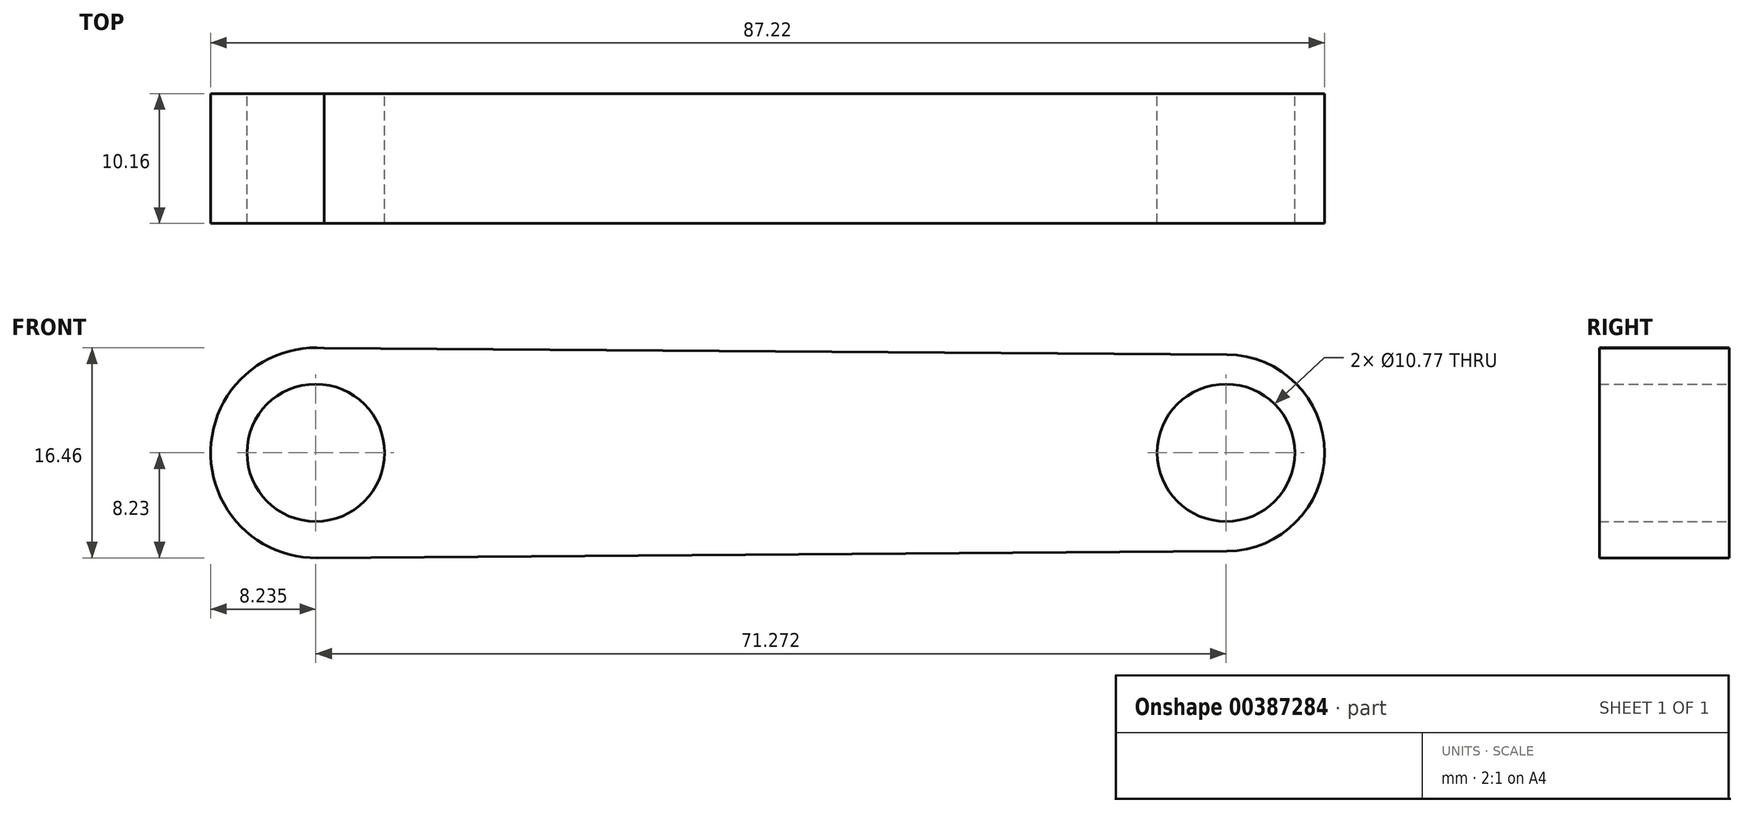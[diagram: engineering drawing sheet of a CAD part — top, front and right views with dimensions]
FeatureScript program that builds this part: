
annotation { "Feature Type Name" : "Feature", "Feature Type Description" : "" }
export const myFeature = defineFeature(function(context is Context, id is Id, definition is map)
    precondition{}
    {
        {
            var Q0;
            Q0=qCreatedBy(makeId("Front.planeOp"),FACE);
            var sketch = newSketch(context, id + "F0", { "sketchPlane" : qUnion([Q0])});
            skCircle(sketch, "E0", {"center": v(-39.6, 0) * mm, "radius": 5.39 * mm});
            skCircle(sketch, "E1", {"center": v(31.68, 0) * mm, "radius": 5.39 * mm});
            skArc(sketch, "E2", {"start": v(-38.94, 8.2) * mm, "mid": v(-47.82, 0.26) * mm, "end": v(-39.47, -8.23) * mm});
            skArc(sketch, "E3", {"start": v(31.73, -7.7) * mm, "mid": v(39.39, 0) * mm, "end": v(31.73, 7.7) * mm});
            skLineSegment(sketch, "E4", {"start": v(-40.13, 8.22) * mm, "end": v(31.73, 7.7) * mm});
            skLineSegment(sketch, "E5", {"start": v(-39.6, -8.23) * mm, "end": v(31.73, -7.7) * mm});
            skSolve(sketch);
        }
        {
            var Q0;
            Q0 = qSketchRegion(id + "F0", true);
            extrude(context, id + "F1", {"entities" : qUnion([Q0]), "depth" : 10.16 * mm});
        }
    });
